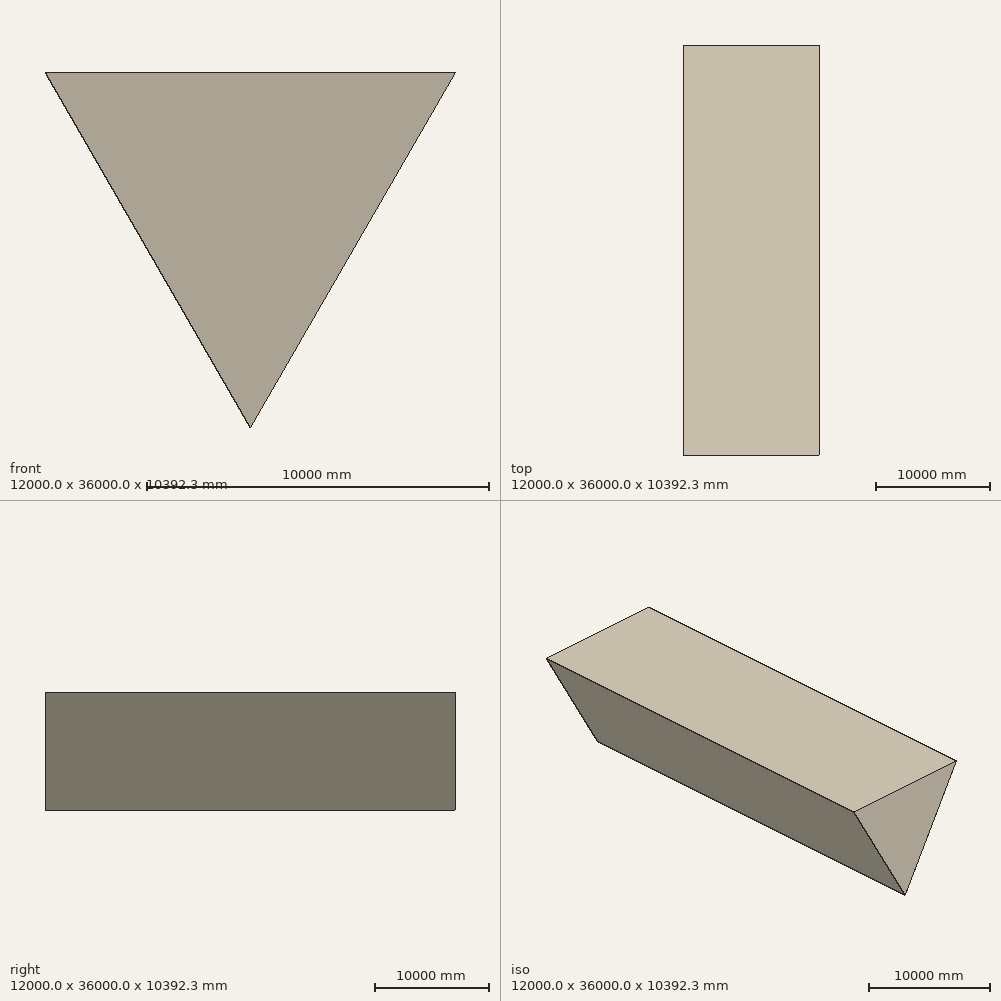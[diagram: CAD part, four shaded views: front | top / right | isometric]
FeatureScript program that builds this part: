
annotation { "Feature Type Name" : "Feature", "Feature Type Description" : "" }
export const myFeature = defineFeature(function(context is Context, id is Id, definition is map)
    precondition{}
    {
        {
            var Q0;
            Q0=qCreatedBy(makeId("Front.planeOp"),FACE);
            var sketch = newSketch(context, id + "F0", { "sketchPlane" : qUnion([Q0])});
            skLineSegment(sketch, "E0", {"start": v(-5953.52, 5227.9) * mm, "end": v(6046.48, 5227.9) * mm});
            skLineSegment(sketch, "E1", {"start": v(6046.48, 5227.9) * mm, "end": v(46.48, -5164.4) * mm});
            skLineSegment(sketch, "E2", {"start": v(46.48, -5164.4) * mm, "end": v(-5953.52, 5227.9) * mm});
            skSolve(sketch);
        }
        {
            var Q0;
            Q0 = qSketchRegion(id + "F0", true);
            extrude(context, id + "F1", {"entities" : qUnion([Q0]), "oppositeDirection" : true, "depth" : 36000 * mm, "offsetDistance" : 25 * mm});
        }
    });
